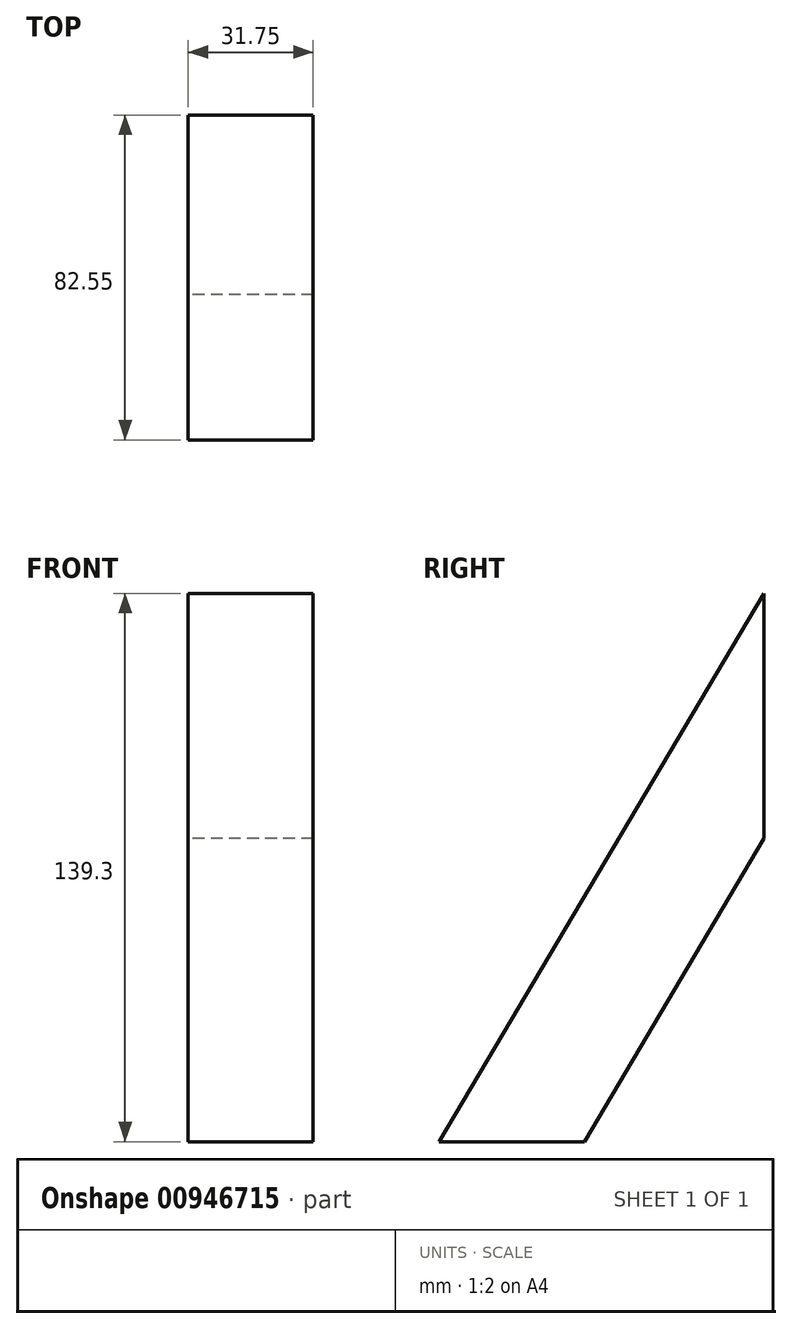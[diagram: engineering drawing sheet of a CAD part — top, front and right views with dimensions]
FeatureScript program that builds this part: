
annotation { "Feature Type Name" : "Feature", "Feature Type Description" : "" }
export const myFeature = defineFeature(function(context is Context, id is Id, definition is map)
    precondition{}
    {
        {
            var Q0;
            Q0=qCreatedBy(makeId("Right.planeOp"),FACE);
            var sketch = newSketch(context, id + "F0", { "sketchPlane" : qUnion([Q0])});
            skLineSegment(sketch, "E0.top", {"start": v(-64.7, -171.45) * mm, "end": v(-101.6, -171.45) * mm});
            skPoint(sketch, "E0.middle", {"position": v(0, 0) * mm});
            skLineSegment(sketch, "E1", {"start": v(-101.6, -171.45) * mm, "end": v(0, 0) * mm});
            skLineSegment(sketch, "E2.0", {"start": v(-64.7, -171.45) * mm, "end": v(-19.05, -94.43) * mm});
            skPoint(sketch, "E0.bottom.end.orphan", {"position": v(-101.6, 171.45) * mm});
            skLineSegment(sketch, "E3", {"start": v(-101.6, -171.45) * mm, "end": v(-64.7, -171.45) * mm});
            skLineSegment(sketch, "E4", {"start": v(-19.05, -94.43) * mm, "end": v(-19.05, -32.15) * mm});
            skPoint(sketch, "E0.left.end.orphan", {"position": v(101.6, -171.45) * mm});
            skPoint(sketch, "E0.left.start.orphan", {"position": v(101.6, 171.45) * mm});
            skPoint(sketch, "E5.orphan", {"position": v(-19.05, -171.45) * mm});
            skSolve(sketch);
        }
        {
            var Q0;
            Q0 = qSketchRegion(id + "F0", true);
            extrude(context, id + "F1", {"entities" : qUnion([Q0]), "depth" : 31.75 * mm, "offsetDistance" : 25.4 * mm});
        }
    });
